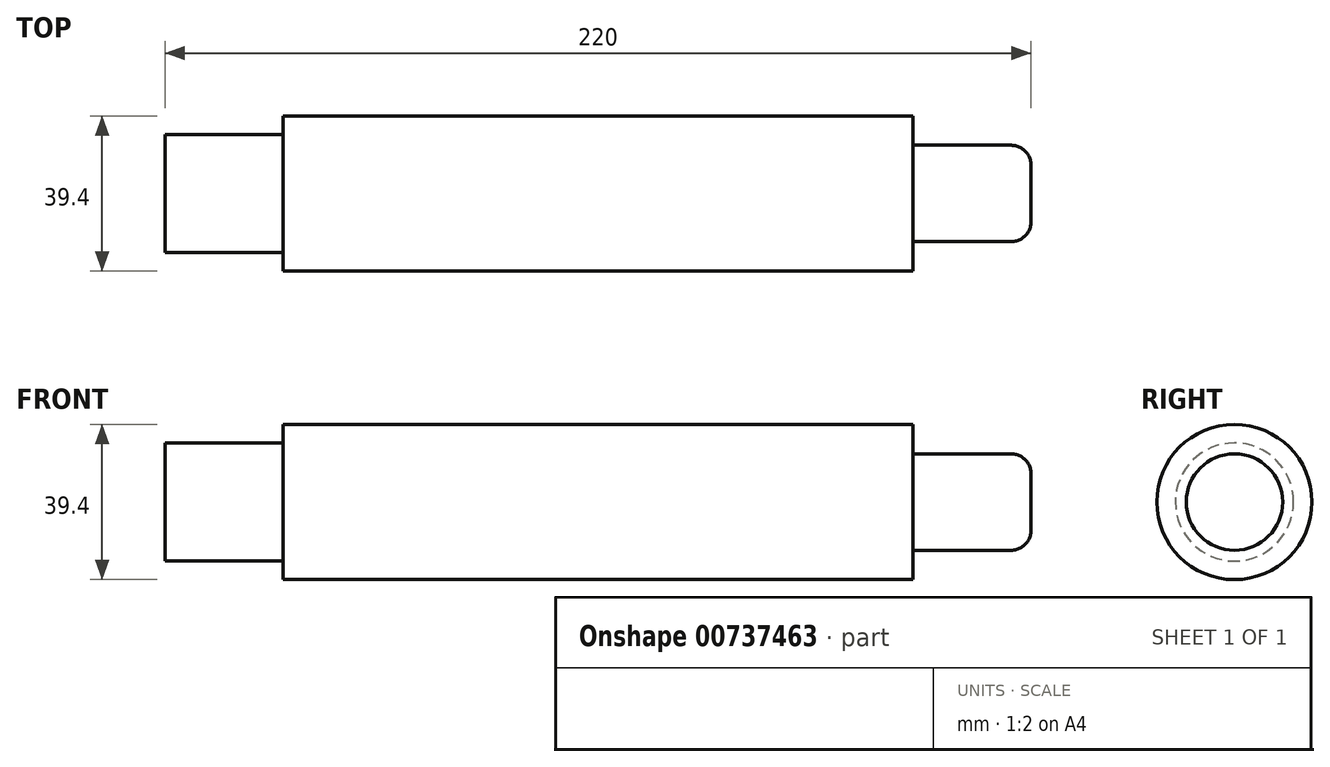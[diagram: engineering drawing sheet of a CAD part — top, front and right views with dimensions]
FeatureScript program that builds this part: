
annotation { "Feature Type Name" : "Feature", "Feature Type Description" : "" }
export const myFeature = defineFeature(function(context is Context, id is Id, definition is map)
    precondition{}
    {
        {
            var Q0;
            Q0=qCreatedBy(makeId("Front.planeOp"),FACE);
            var sketch = newSketch(context, id + "F0", { "sketchPlane" : qUnion([Q0])});
            skLineSegment(sketch, "E0.bottom", {"start": v(-71.53, 15) * mm, "end": v(-41.53, 15) * mm});
            skLineSegment(sketch, "E0.left", {"start": v(-71.53, 15) * mm, "end": v(-71.53, 0) * mm});
            skLineSegment(sketch, "E1.bottom", {"start": v(-41.53, 19.7) * mm, "end": v(118.47, 19.7) * mm});
            skLineSegment(sketch, "E1.left", {"start": v(-41.53, 19.7) * mm, "end": v(-41.53, 15) * mm});
            skLineSegment(sketch, "E1.right", {"start": v(118.47, 19.7) * mm, "end": v(118.47, 12.25) * mm});
            skLineSegment(sketch, "E2.bottom", {"start": v(118.47, 12.25) * mm, "end": v(148.47, 12.25) * mm});
            skLineSegment(sketch, "E2.right", {"start": v(148.47, 12.25) * mm, "end": v(148.47, 0) * mm});
            skLineSegment(sketch, "E3", {"start": v(-65.77, 0) * mm, "end": v(81.57, 0) * mm, "construction": true});
            skLineSegment(sketch, "E4", {"start": v(-71.53, 0) * mm, "end": v(148.47, 0) * mm});
            skSolve(sketch);
        }
        {
            var Q0;
            Q0 = qSketchRegion(id + "F0", true);
            var Q1;
            Q1=sQuery(id+"F0.wireOp",EDGE,"E3");
            revolve(context, id + "F1", {"surfaceOperationType" : NewSurfaceOperationType.NEW, "entities" : qUnion([Q0]), "axis" : qUnion([Q1]), "revolveType" : RevolveType.FULL});
        }
        {
            var Q0;
            Q0=makeQuery(id+"F1.opRevolve","SWEPT_FACE",FACE,{"disambiguationData":[OSD([sQuery(id+"F0.wireOp",EDGE,"E2.right")])]});
            fillet(context, id + "F2", {"entities" : qUnion([Q0]), "radius" : 5 * mm, "tangentPropagation" : true, "allowEdgeOverflow" : false});
        }
    });
